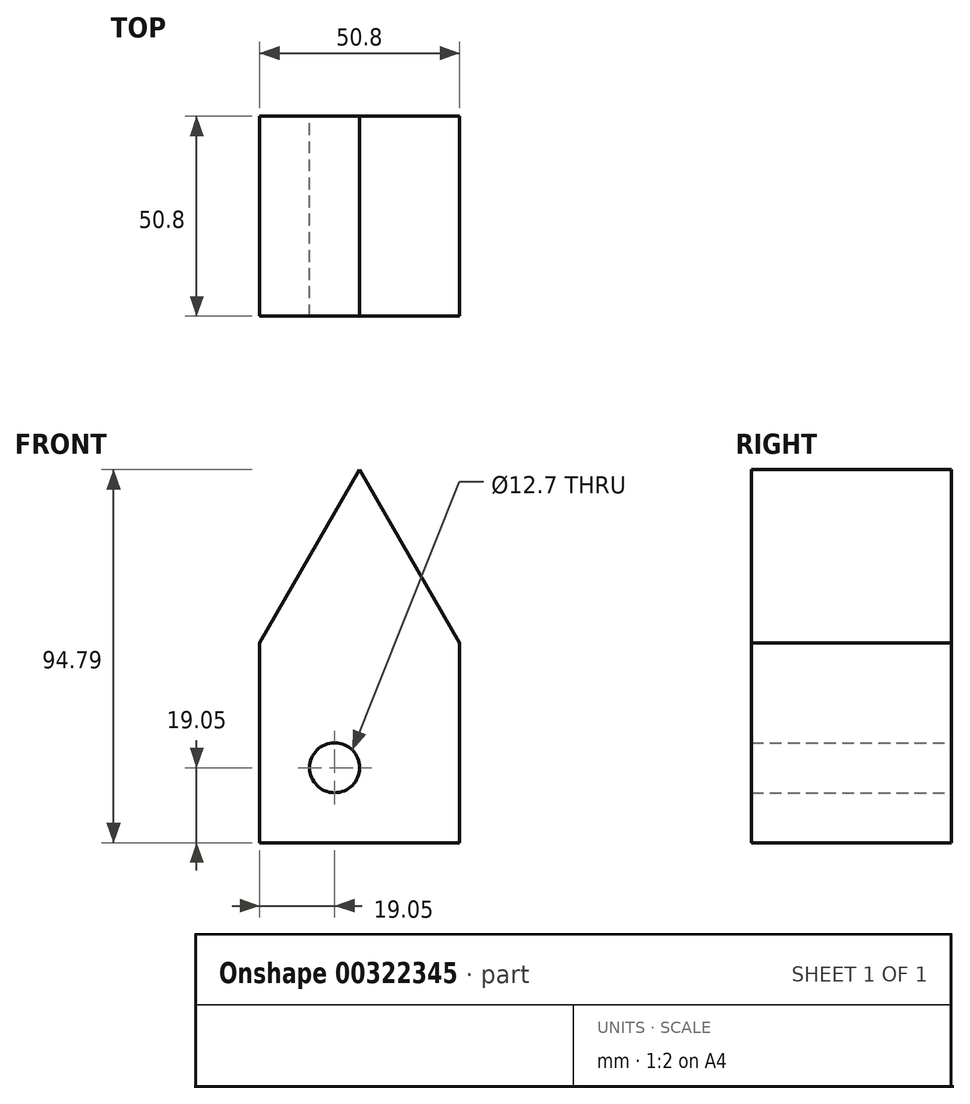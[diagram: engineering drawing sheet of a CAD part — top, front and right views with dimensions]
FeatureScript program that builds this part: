
annotation { "Feature Type Name" : "Feature", "Feature Type Description" : "" }
export const myFeature = defineFeature(function(context is Context, id is Id, definition is map)
    precondition{}
    {
        {
            var Q0;
            Q0=qCreatedBy(makeId("Front.planeOp"),FACE);
            var sketch = newSketch(context, id + "F0", { "sketchPlane" : qUnion([Q0])});
            skLineSegment(sketch, "E0.bottom", {"start": v(25.4, -25.4) * mm, "end": v(-25.4, -25.4) * mm});
            skLineSegment(sketch, "E0.left", {"start": v(25.4, -25.4) * mm, "end": v(25.4, 25.4) * mm});
            skLineSegment(sketch, "E0.right", {"start": v(-25.4, -25.4) * mm, "end": v(-25.4, 25.4) * mm});
            skPoint(sketch, "E0.middle", {"position": v(0, 0) * mm});
            skLineSegment(sketch, "E1", {"start": v(-25.4, 25.4) * mm, "end": v(0, 69.4) * mm});
            skLineSegment(sketch, "E2", {"start": v(25.4, 25.4) * mm, "end": v(0, 69.4) * mm});
            skCircle(sketch, "E3", {"center": v(-6.35, -6.35) * mm, "radius": 6.35 * mm});
            skSolve(sketch);
        }
        {
            var Q0;
            Q0=makeQuery(id+"F0.imprint","IMPRINT",FACE,{"disambiguationData":[TD([[makeQuery(id+"F0.imprint","IMPRINT",EDGE,{"derivedFrom":sQuery(id+"F0.wireOp",EDGE,"E0.bottom")}),-1.0]])]});
            extrude(context, id + "F1", {"entities" : qUnion([Q0]), "depth" : 50.8 * mm});
        }
    });
